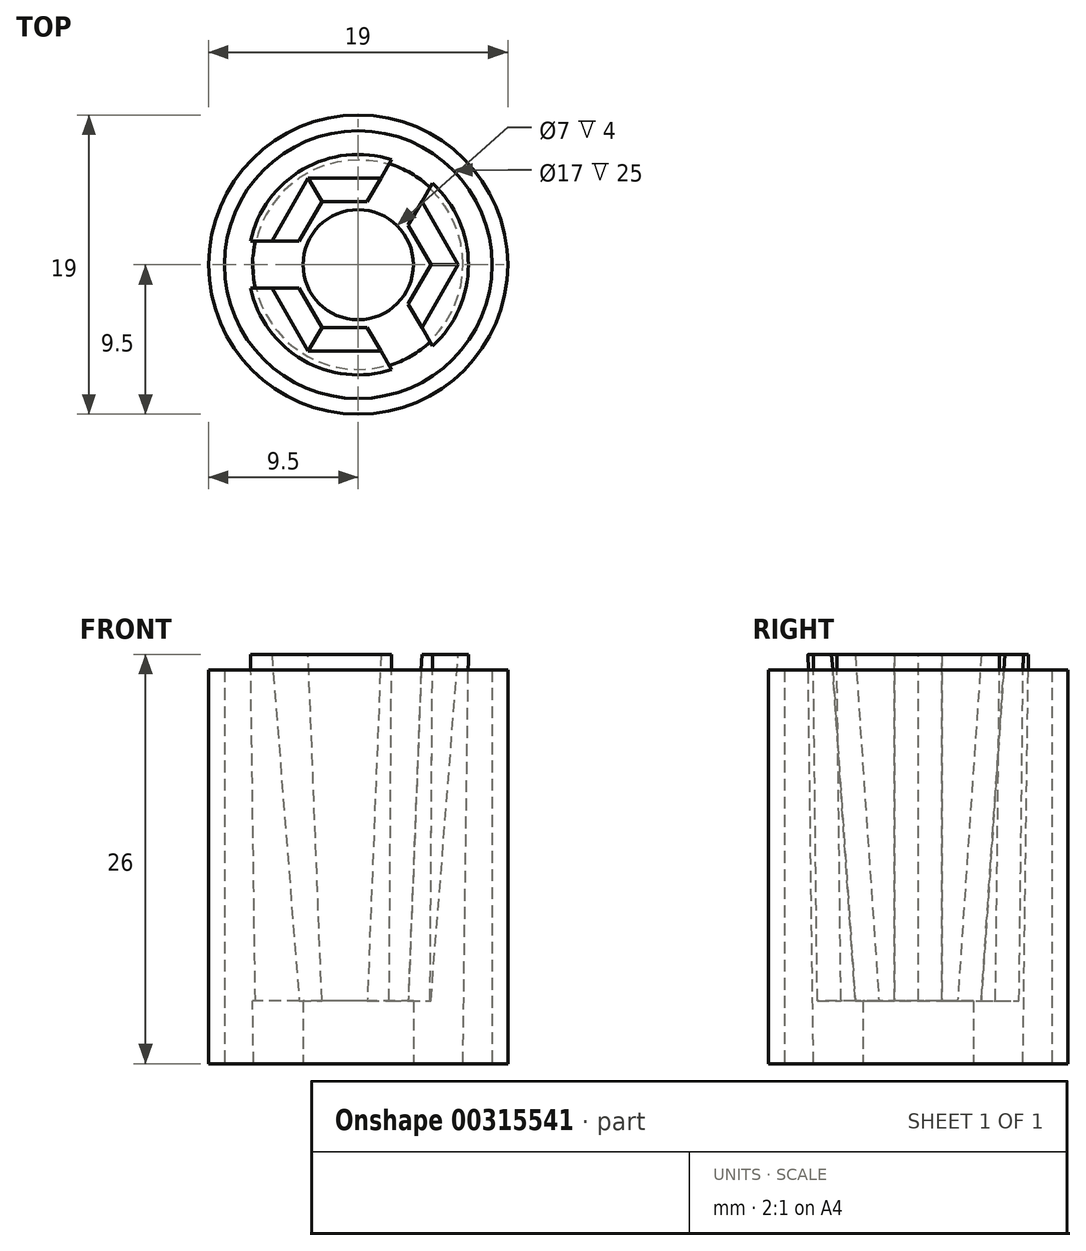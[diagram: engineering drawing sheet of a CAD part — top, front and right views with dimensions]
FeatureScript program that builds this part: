
annotation { "Feature Type Name" : "Feature", "Feature Type Description" : "" }
export const myFeature = defineFeature(function(context is Context, id is Id, definition is map)
    precondition{}
    {
        {
            var Q0;
            Q0=qCreatedBy(makeId("Top.planeOp"),FACE);
            cPlane(context, id + "F0", {"entities" : qUnion([Q0]), "cplaneType" : CPlaneType.OFFSET, "offset" : 26 * mm, "width" : 150 * mm, "height" : 150 * mm});
        }
        {
            var Q0;
            Q0=qCreatedBy(makeId("Top.planeOp"),FACE);
            var sketch = newSketch(context, id + "F1", { "sketchPlane" : qUnion([Q0])});
            skCircle(sketch, "E0", {"center": v(0, 0) * mm, "radius": 6.65 * mm});
            skSolve(sketch);
        }
        {
            var Q0;
            Q0=qCreatedBy(makeId("Top.planeOp"),FACE);
            var sketch = newSketch(context, id + "F2", { "sketchPlane" : qUnion([Q0])});
            skCircle(sketch, "E1", {"center": v(0, 0) * mm, "radius": 3.5 * mm});
            skSolve(sketch);
        }
        {
            var Q0;
            Q0=qCreatedBy(id+"F0.planeOp",FACE);
            var sketch = newSketch(context, id + "F3", { "sketchPlane" : qUnion([Q0])});
            skCircle(sketch, "E2", {"center": v(0, 0) * mm, "radius": 7 * mm});
            skSolve(sketch);
        }
        {
            var Q0;
            Q0=makeQuery(id+"F1.imprint","IMPRINT",FACE,{"disambiguationData":[TD([[makeQuery(id+"F1.imprint","IMPRINT",EDGE,{"derivedFrom":sQuery(id+"F1.wireOp",EDGE,"E0")}),1.0]])]});
            var Q1;
            Q1=makeQuery(id+"F3.imprint","IMPRINT",FACE,{"disambiguationData":[TD([[makeQuery(id+"F3.imprint","IMPRINT",EDGE,{"derivedFrom":sQuery(id+"F3.wireOp",EDGE,"E2")}),1.0]])]});
            loft(context, id + "F4", {"sheetProfilesArray" : [{ "sheetProfileEntities" : qUnion([Q0]) }, { "sheetProfileEntities" : qUnion([Q1]) }]});
        }
        {
            var Q0;
            Q0=makeQuery(id+"F2.imprint","IMPRINT",FACE,{"disambiguationData":[TD([[makeQuery(id+"F2.imprint","IMPRINT",EDGE,{"derivedFrom":sQuery(id+"F2.wireOp",EDGE,"E1")}),1.0]])]});
            extrude(context, id + "F5", {"entities" : qUnion([Q0]), "operationType" : NewBodyOperationType.REMOVE, "depth" : 32 * mm});
        }
        {
            var Q0;
            Q0=qCreatedBy(makeId("Top.planeOp"),FACE);
            cPlane(context, id + "F6", {"entities" : qUnion([Q0]), "cplaneType" : CPlaneType.OFFSET, "offset" : 4 * mm, "width" : 150 * mm, "height" : 150 * mm});
        }
        {
            var Q0;
            Q0=qCreatedBy(id+"F6.planeOp",FACE);
            var sketch = newSketch(context, id + "F7", { "sketchPlane" : qUnion([Q0])});
            skCircle(sketch, "E3.cCircle", {"center": v(0, 0) * mm, "radius": 4 * mm, "construction": true});
            skLineSegment(sketch, "E3.0", {"start": v(-4.62, 0) * mm, "end": v(-2.3, 4) * mm});
            skLineSegment(sketch, "E3.1", {"start": v(-2.3, 4) * mm, "end": v(2.3, 4) * mm});
            skLineSegment(sketch, "E3.2", {"start": v(2.3, 4) * mm, "end": v(4.62, 0) * mm});
            skLineSegment(sketch, "E3.3", {"start": v(4.62, 0) * mm, "end": v(2.3, -4) * mm});
            skLineSegment(sketch, "E3.4", {"start": v(2.3, -4) * mm, "end": v(-2.3, -4) * mm});
            skLineSegment(sketch, "E3.5", {"start": v(-2.3, -4) * mm, "end": v(-4.62, 0) * mm});
            skPoint(sketch, "E3.0.midPoint", {"position": v(-3.46, 2) * mm});
            skSolve(sketch);
        }
        {
            var Q0;
            Q0=qCreatedBy(id+"F0.planeOp",FACE);
            var sketch = newSketch(context, id + "F8", { "sketchPlane" : qUnion([Q0])});
            skCircle(sketch, "E4.cCircle", {"center": v(0, 0) * mm, "radius": 5.5 * mm, "construction": true});
            skLineSegment(sketch, "E4.0", {"start": v(3.18, 5.5) * mm, "end": v(6.35, 0) * mm});
            skLineSegment(sketch, "E4.1", {"start": v(6.35, 0) * mm, "end": v(3.18, -5.5) * mm});
            skLineSegment(sketch, "E4.2", {"start": v(3.18, -5.5) * mm, "end": v(-3.18, -5.5) * mm});
            skLineSegment(sketch, "E4.3", {"start": v(-3.18, -5.5) * mm, "end": v(-6.35, 0) * mm});
            skLineSegment(sketch, "E4.4", {"start": v(-6.35, 0) * mm, "end": v(-3.18, 5.5) * mm});
            skLineSegment(sketch, "E4.5", {"start": v(-3.18, 5.5) * mm, "end": v(3.18, 5.5) * mm});
            skPoint(sketch, "E4.0.midPoint", {"position": v(4.76, 2.75) * mm});
            skSolve(sketch);
        }
        {
            var Q0;
            Q0=qCreatedBy(id+"F6.planeOp",FACE);
            var sketch = newSketch(context, id + "F9", { "sketchPlane" : qUnion([Q0])});
            skLineSegment(sketch, "E5.bottom", {"start": v(-1.37, 1.5) * mm, "end": v(-11.37, 1.5) * mm});
            skLineSegment(sketch, "E5.top", {"start": v(-1.37, -1.5) * mm, "end": v(-11.37, -1.5) * mm});
            skLineSegment(sketch, "E5.left", {"start": v(-1.37, 1.5) * mm, "end": v(-1.37, -1.5) * mm});
            skLineSegment(sketch, "E5.right", {"start": v(-11.37, 1.5) * mm, "end": v(-11.37, -1.5) * mm});
            skLineSegment(sketch, "E6.1.0", {"start": v(4.38, -10.6) * mm, "end": v(6.98, -9.1) * mm});
            skLineSegment(sketch, "E6.1.1", {"start": v(-0.62, -1.93) * mm, "end": v(4.38, -10.6) * mm});
            skLineSegment(sketch, "E6.1.2", {"start": v(-0.62, -1.93) * mm, "end": v(1.98, -0.43) * mm});
            skLineSegment(sketch, "E6.1.3", {"start": v(1.98, -0.43) * mm, "end": v(6.98, -9.1) * mm});
            skLineSegment(sketch, "E6.2.0", {"start": v(6.98, 9.1) * mm, "end": v(4.38, 10.6) * mm});
            skLineSegment(sketch, "E6.2.1", {"start": v(1.98, 0.43) * mm, "end": v(6.98, 9.1) * mm});
            skLineSegment(sketch, "E6.2.2", {"start": v(1.98, 0.43) * mm, "end": v(-0.62, 1.93) * mm});
            skLineSegment(sketch, "E6.2.3", {"start": v(-0.62, 1.93) * mm, "end": v(4.38, 10.6) * mm});
            skPoint(sketch, "E6.center", {"position": v(0, 0) * mm});
            skSolve(sketch);
        }
        {
            var Q1;
            Q1 = qSketchRegion(id + "F7", true);
            var Q2;
            Q2 = qSketchRegion(id + "F8", true);
            loft(context, id + "F10", {"operationType" : NewBodyOperationType.REMOVE, "sheetProfilesArray" : [{ "sheetProfileEntities" : qUnion([Q1]) }, { "sheetProfileEntities" : qUnion([Q2]) }]});
        }
        {
            var Q0;
            Q0 = qSketchRegion(id + "F9", true);
            extrude(context, id + "F11", {"entities" : qUnion([Q0]), "operationType" : NewBodyOperationType.REMOVE, "depth" : 25 * mm});
        }
        {
            var Q0;
            Q0=qCreatedBy(makeId("Top.planeOp"),FACE);
            var sketch = newSketch(context, id + "F12", { "sketchPlane" : qUnion([Q0])});
            skCircle(sketch, "E7", {"center": v(0, 0) * mm, "radius": 8.5 * mm});
            skCircle(sketch, "E8", {"center": v(0, 0) * mm, "radius": 9.5 * mm});
            skSolve(sketch);
        }
        {
            var Q0;
            Q0=makeQuery(id+"F12.imprint","IMPRINT",FACE,{"disambiguationData":[TD([[makeQuery(id+"F12.imprint","IMPRINT",EDGE,{"derivedFrom":sQuery(id+"F12.wireOp",EDGE,"E7")}),-1.0]])]});
            extrude(context, id + "F13", {"entities" : qUnion([Q0]), "depth" : 25 * mm});
        }
    });
